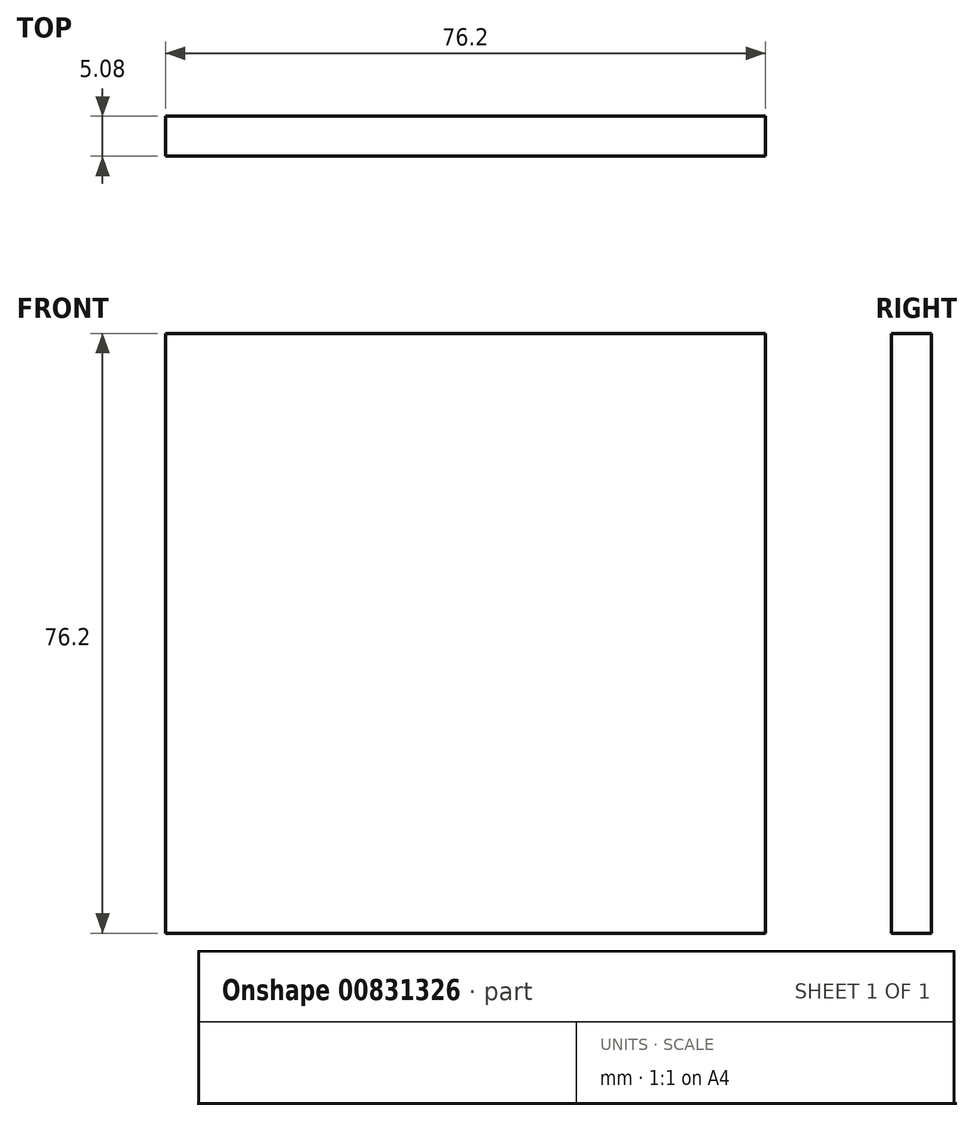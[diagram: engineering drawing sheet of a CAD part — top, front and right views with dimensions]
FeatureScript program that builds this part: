
annotation { "Feature Type Name" : "Feature", "Feature Type Description" : "" }
export const myFeature = defineFeature(function(context is Context, id is Id, definition is map)
    precondition{}
    {
        {
            var Q0;
            Q0=qCreatedBy(makeId("Front.planeOp"),FACE);
            var sketch = newSketch(context, id + "F0", { "sketchPlane" : qUnion([Q0])});
            skLineSegment(sketch, "E0", {"start": v(0, 0) * mm, "end": v(0, 76.2) * mm});
            skLineSegment(sketch, "E1", {"start": v(0, 76.2) * mm, "end": v(76.2, 76.2) * mm});
            skLineSegment(sketch, "E2", {"start": v(76.2, 76.2) * mm, "end": v(76.2, 0) * mm});
            skLineSegment(sketch, "E3", {"start": v(76.2, 0) * mm, "end": v(0, 0) * mm});
            skSolve(sketch);
        }
        {
            var Q0;
            Q0=makeQuery(id+"F0.imprint","IMPRINT",FACE,{"disambiguationData":[TD([[makeQuery(id+"F0.imprint","IMPRINT",EDGE,{"derivedFrom":sQuery(id+"F0.wireOp",EDGE,"E0")}),-1.0]])]});
            extrude(context, id + "F1", {"entities" : qUnion([Q0]), "depth" : 5.08 * mm, "offsetDistance" : 25.4 * mm});
        }
    });
